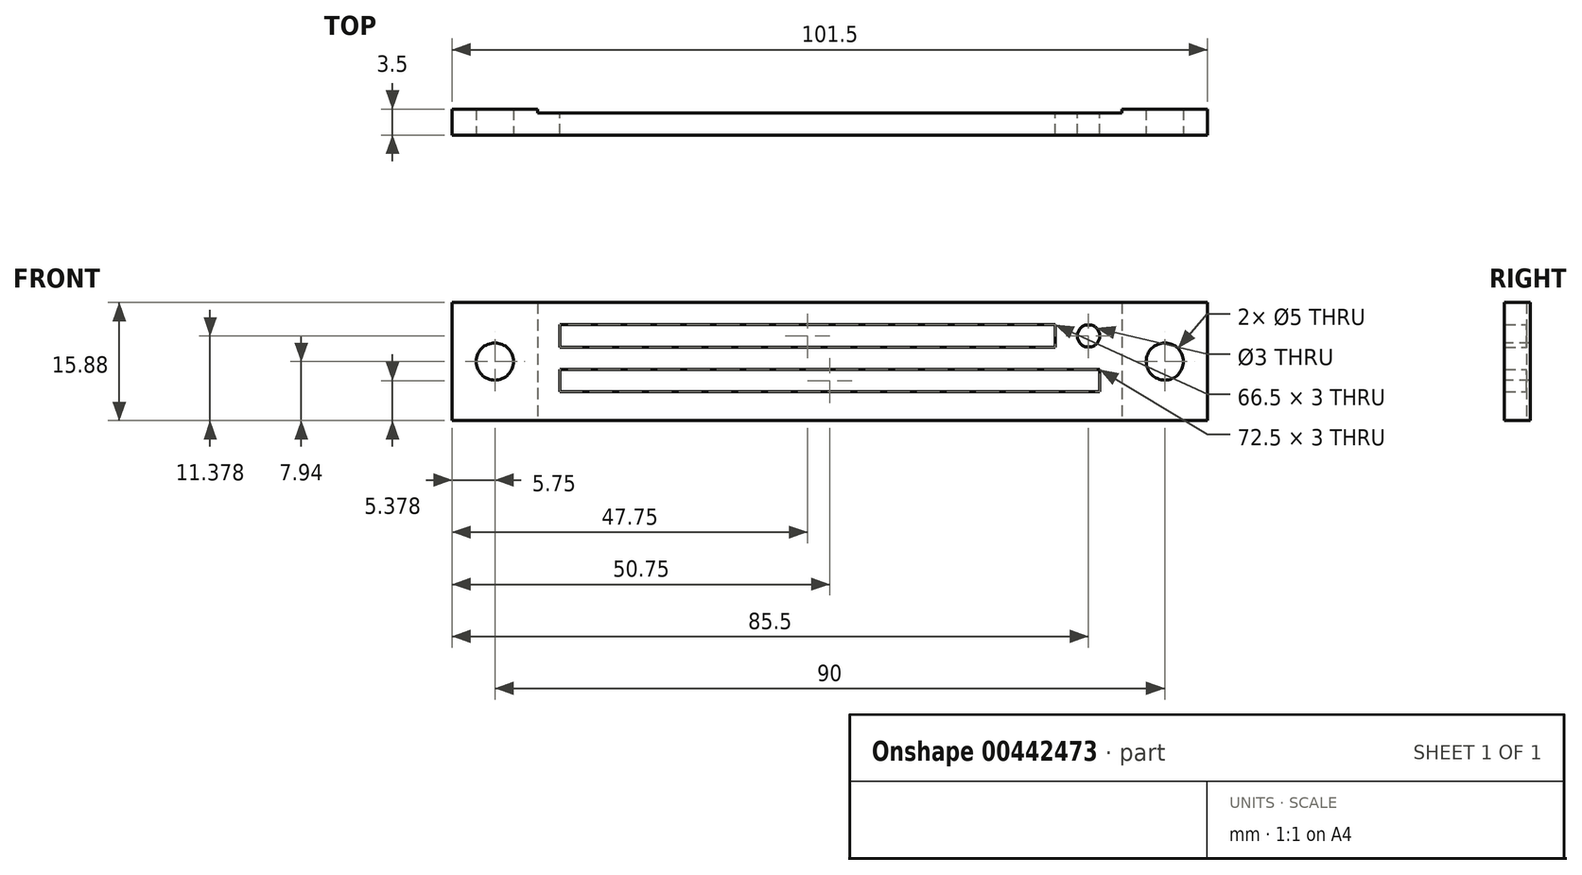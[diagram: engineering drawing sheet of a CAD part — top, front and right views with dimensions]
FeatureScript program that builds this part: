
annotation { "Feature Type Name" : "Feature", "Feature Type Description" : "" }
export const myFeature = defineFeature(function(context is Context, id is Id, definition is map)
    precondition{}
    {
        {
            var Q0;
            Q0=qCreatedBy(makeId("Front.planeOp"),FACE);
            var sketch = newSketch(context, id + "F0", { "sketchPlane" : qUnion([Q0])});
            skLineSegment(sketch, "E0.bottom", {"start": v(50.75, 7.94) * mm, "end": v(-50.75, 7.94) * mm});
            skLineSegment(sketch, "E0.top", {"start": v(50.75, -7.94) * mm, "end": v(-50.75, -7.94) * mm});
            skLineSegment(sketch, "E0.left", {"start": v(50.75, 7.94) * mm, "end": v(50.75, -7.94) * mm});
            skLineSegment(sketch, "E0.right", {"start": v(-50.75, 7.94) * mm, "end": v(-50.75, -7.94) * mm});
            skPoint(sketch, "E0.middle", {"position": v(0, 0) * mm});
            skLineSegment(sketch, "E1.bottom", {"start": v(39.25, 7.94) * mm, "end": v(-39.25, 7.94) * mm, "construction": true});
            skLineSegment(sketch, "E1.top", {"start": v(39.25, -7.94) * mm, "end": v(-39.25, -7.94) * mm, "construction": true});
            skLineSegment(sketch, "E1.left", {"start": v(39.25, 7.94) * mm, "end": v(39.25, -7.94) * mm, "construction": true});
            skLineSegment(sketch, "E1.right", {"start": v(-39.25, 7.94) * mm, "end": v(-39.25, -7.94) * mm, "construction": true});
            skLineSegment(sketch, "E2.bottom", {"start": v(-36.25, 4.94) * mm, "end": v(30.25, 4.94) * mm});
            skLineSegment(sketch, "E2.top", {"start": v(-36.25, 1.94) * mm, "end": v(30.25, 1.94) * mm});
            skLineSegment(sketch, "E2.left", {"start": v(-36.25, 4.94) * mm, "end": v(-36.25, 1.94) * mm});
            skLineSegment(sketch, "E2.right", {"start": v(30.25, 4.94) * mm, "end": v(30.25, 1.94) * mm});
            skLineSegment(sketch, "E3.bottom", {"start": v(-36.25, -1.06) * mm, "end": v(36.25, -1.06) * mm});
            skLineSegment(sketch, "E3.top", {"start": v(-36.25, -4.06) * mm, "end": v(36.25, -4.06) * mm});
            skLineSegment(sketch, "E3.left", {"start": v(-36.25, -1.06) * mm, "end": v(-36.25, -4.06) * mm});
            skLineSegment(sketch, "E3.right", {"start": v(36.25, -1.06) * mm, "end": v(36.25, -4.06) * mm});
            skCircle(sketch, "E4", {"center": v(34.75, 3.44) * mm, "radius": 1.5 * mm});
            skSolve(sketch);
        }
        {
            var Q0;
            Q0 = qSketchRegion(id + "F0", true);
            extrude(context, id + "F1", {"entities" : qUnion([Q0]), "depth" : 3.5 * mm});
        }
        {
            var Q0;
            Q0=makeQuery(id+"F1.opExtrude","CAP_FACE",FACE,{"disambiguationData":[OSD([sQuery(id+"F0.wireOp",EDGE,"E0.bottom"),sQuery(id+"F0.wireOp",EDGE,"E0.top"),sQuery(id+"F0.wireOp",EDGE,"E0.left"),sQuery(id+"F0.wireOp",EDGE,"E0.right"),sQuery(id+"F0.wireOp",EDGE,"E2.bottom"),sQuery(id+"F0.wireOp",EDGE,"E2.top"),sQuery(id+"F0.wireOp",EDGE,"E2.left"),sQuery(id+"F0.wireOp",EDGE,"E2.right"),sQuery(id+"F0.wireOp",EDGE,"E3.bottom"),sQuery(id+"F0.wireOp",EDGE,"E3.top"),sQuery(id+"F0.wireOp",EDGE,"E3.left"),sQuery(id+"F0.wireOp",EDGE,"E3.right"),sQuery(id+"F0.wireOp",EDGE,"E4")])],"isStart":true});
            var sketch = newSketch(context, id + "F2", { "sketchPlane" : qUnion([Q0])});
            skLineSegment(sketch, "E5.bottom", {"start": v(39.25, 7.94) * mm, "end": v(-39.25, 7.94) * mm});
            skLineSegment(sketch, "E5.top", {"start": v(39.25, -7.94) * mm, "end": v(-39.25, -7.94) * mm});
            skLineSegment(sketch, "E5.left", {"start": v(39.25, 7.94) * mm, "end": v(39.25, -7.94) * mm});
            skLineSegment(sketch, "E5.right", {"start": v(-39.25, 7.94) * mm, "end": v(-39.25, -7.94) * mm});
            skPoint(sketch, "E5.middle", {"position": v(0, 0) * mm});
            skSolve(sketch);
        }
        {
            var Q0;
            Q0 = qSketchRegion(id + "F2", true);
            extrude(context, id + "F3", {"entities" : qUnion([Q0]), "operationType" : NewBodyOperationType.REMOVE, "oppositeDirection" : true, "depth" : .5 * mm});
        }
        {
            var Q0;
            Q0=makeQuery(id+"F1.opExtrude","CAP_FACE",FACE,{"disambiguationData":[OSD([sQuery(id+"F0.wireOp",EDGE,"E0.bottom"),sQuery(id+"F0.wireOp",EDGE,"E0.top"),sQuery(id+"F0.wireOp",EDGE,"E0.left"),sQuery(id+"F0.wireOp",EDGE,"E0.right"),sQuery(id+"F0.wireOp",EDGE,"E2.bottom"),sQuery(id+"F0.wireOp",EDGE,"E2.top"),sQuery(id+"F0.wireOp",EDGE,"E2.left"),sQuery(id+"F0.wireOp",EDGE,"E2.right"),sQuery(id+"F0.wireOp",EDGE,"E3.bottom"),sQuery(id+"F0.wireOp",EDGE,"E3.top"),sQuery(id+"F0.wireOp",EDGE,"E3.left"),sQuery(id+"F0.wireOp",EDGE,"E3.right"),sQuery(id+"F0.wireOp",EDGE,"E4")])],"isStart":false});
            var sketch = newSketch(context, id + "F4", { "sketchPlane" : qUnion([Q0])});
            skLineSegment(sketch, "E6.bottom", {"start": v(39.25, 7.94) * mm, "end": v(-39.25, 7.94) * mm, "construction": true});
            skLineSegment(sketch, "E6.top", {"start": v(39.25, -7.94) * mm, "end": v(-39.25, -7.94) * mm, "construction": true});
            skLineSegment(sketch, "E6.left", {"start": v(39.25, 7.94) * mm, "end": v(39.25, -7.94) * mm, "construction": true});
            skLineSegment(sketch, "E6.right", {"start": v(-39.25, 7.94) * mm, "end": v(-39.25, -7.94) * mm, "construction": true});
            skPoint(sketch, "E6.middle", {"position": v(0, 0) * mm});
            skLineSegment(sketch, "E7", {"start": v(-50.75, 7.94) * mm, "end": v(-39.25, -7.94) * mm, "construction": true});
            skLineSegment(sketch, "E8", {"start": v(39.25, -7.94) * mm, "end": v(50.75, 7.94) * mm, "construction": true});
            skCircle(sketch, "E9", {"center": v(-45, 0) * mm, "radius": 2.5 * mm});
            skCircle(sketch, "E10", {"center": v(45, 0) * mm, "radius": 2.5 * mm});
            skSolve(sketch);
        }
        {
            var Q0;
            Q0 = qSketchRegion(id + "F4", true);
            extrude(context, id + "F5", {"entities" : qUnion([Q0]), "operationType" : NewBodyOperationType.REMOVE, "oppositeDirection" : true, "depth" : 25 * mm});
        }
    });
